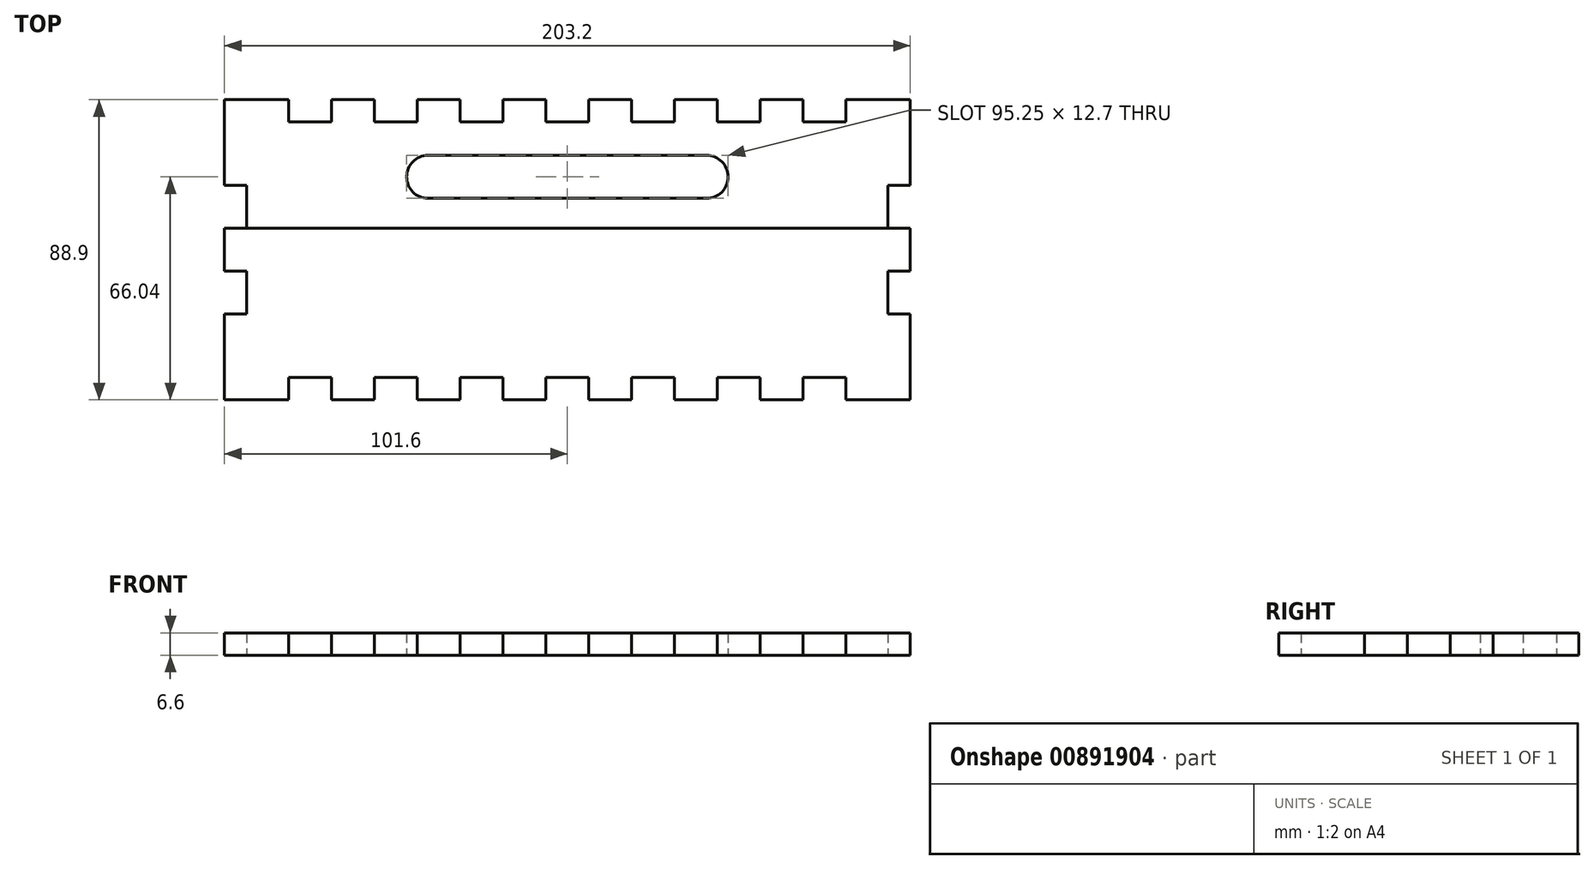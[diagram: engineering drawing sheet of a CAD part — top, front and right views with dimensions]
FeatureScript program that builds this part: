
annotation { "Feature Type Name" : "Feature", "Feature Type Description" : "" }
export const myFeature = defineFeature(function(context is Context, id is Id, definition is map)
    precondition{}
    {
        {
            var Q0;
            Q0=qCreatedBy(makeId("Top.planeOp"),FACE);
            var sketch = newSketch(context, id + "F0", { "sketchPlane" : qUnion([Q0])});
            skLineSegment(sketch, "E0.bottom", {"start": v(0, 0) * mm, "end": v(19.05, 0) * mm});
            skLineSegment(sketch, "E0.left", {"start": v(0, 0) * mm, "end": v(0, -25.4) * mm});
            skLineSegment(sketch, "E1", {"start": v(19.05, 0) * mm, "end": v(19.05, -6.6) * mm});
            skLineSegment(sketch, "E2", {"start": v(19.05, -6.6) * mm, "end": v(31.75, -6.6) * mm});
            skLineSegment(sketch, "E3", {"start": v(31.75, -6.6) * mm, "end": v(31.75, 0) * mm});
            skLineSegment(sketch, "E4", {"start": v(31.75, 0) * mm, "end": v(44.45, 0) * mm});
            skLineSegment(sketch, "E5", {"start": v(44.45, 0) * mm, "end": v(44.45, -6.6) * mm});
            skLineSegment(sketch, "E6", {"start": v(44.45, -6.6) * mm, "end": v(57.15, -6.6) * mm});
            skLineSegment(sketch, "E7", {"start": v(57.15, -6.6) * mm, "end": v(57.15, 0) * mm});
            skLineSegment(sketch, "E8", {"start": v(57.15, 0) * mm, "end": v(69.85, 0) * mm});
            skLineSegment(sketch, "E9", {"start": v(69.85, 0) * mm, "end": v(69.85, -6.6) * mm});
            skLineSegment(sketch, "E10", {"start": v(69.85, -6.6) * mm, "end": v(82.55, -6.6) * mm});
            skLineSegment(sketch, "E11", {"start": v(82.55, -6.6) * mm, "end": v(82.55, 0) * mm});
            skLineSegment(sketch, "E12.trimOffspring", {"start": v(82.55, 0) * mm, "end": v(95.25, 0) * mm});
            skLineSegment(sketch, "E13", {"start": v(95.25, 0) * mm, "end": v(95.25, -6.6) * mm});
            skLineSegment(sketch, "E14", {"start": v(95.25, -6.6) * mm, "end": v(107.95, -6.6) * mm});
            skLineSegment(sketch, "E15", {"start": v(107.95, -6.6) * mm, "end": v(107.95, 0) * mm});
            skLineSegment(sketch, "E16", {"start": v(107.95, 0) * mm, "end": v(120.65, 0) * mm});
            skLineSegment(sketch, "E17", {"start": v(120.65, 0) * mm, "end": v(120.65, -6.6) * mm});
            skLineSegment(sketch, "E18", {"start": v(120.65, -6.6) * mm, "end": v(133.35, -6.6) * mm});
            skLineSegment(sketch, "E19", {"start": v(133.35, -6.6) * mm, "end": v(133.35, 0) * mm});
            skLineSegment(sketch, "E20", {"start": v(133.35, 0) * mm, "end": v(146.05, 0) * mm});
            skLineSegment(sketch, "E21", {"start": v(146.05, 0) * mm, "end": v(146.05, -6.6) * mm});
            skLineSegment(sketch, "E22", {"start": v(146.05, -6.6) * mm, "end": v(158.75, -6.6) * mm});
            skLineSegment(sketch, "E23", {"start": v(158.75, -6.6) * mm, "end": v(158.75, 0) * mm});
            skLineSegment(sketch, "E24.trimOffspring", {"start": v(158.75, 0) * mm, "end": v(171.45, 0) * mm});
            skLineSegment(sketch, "E25", {"start": v(171.45, 0) * mm, "end": v(171.45, -6.6) * mm});
            skLineSegment(sketch, "E26", {"start": v(171.45, -6.6) * mm, "end": v(184.15, -6.6) * mm});
            skLineSegment(sketch, "E27", {"start": v(184.15, -6.6) * mm, "end": v(184.15, 0) * mm});
            skLineSegment(sketch, "E28.trimOffspring", {"start": v(184.15, 0) * mm, "end": v(203.2, 0) * mm});
            skLineSegment(sketch, "E29", {"start": v(0, -25.4) * mm, "end": v(6.6, -25.4) * mm});
            skLineSegment(sketch, "E30", {"start": v(6.6, -25.4) * mm, "end": v(6.6, -38.1) * mm});
            skLineSegment(sketch, "E31", {"start": v(6.6, -38.1) * mm, "end": v(0, -38.1) * mm});
            skLineSegment(sketch, "E32", {"start": v(0, -38.1) * mm, "end": v(0, -50.8) * mm});
            skLineSegment(sketch, "E33", {"start": v(0, -50.8) * mm, "end": v(6.6, -50.8) * mm});
            skLineSegment(sketch, "E34", {"start": v(6.6, -50.8) * mm, "end": v(6.6, -63.5) * mm});
            skLineSegment(sketch, "E35", {"start": v(6.6, -63.5) * mm, "end": v(0, -63.5) * mm});
            skLineSegment(sketch, "E36.trimOffspring", {"start": v(0, -63.5) * mm, "end": v(0, -88.9) * mm});
            skLineSegment(sketch, "E37", {"start": v(101.6, -6.6) * mm, "end": v(101.6, -6.6) * mm});
            skLineSegment(sketch, "E38", {"start": v(0, -44.45) * mm, "end": v(0, -44.45) * mm});
            skLineSegment(sketch, "E39.MirrorCS", {"start": v(203.2, 0) * mm, "end": v(203.2, -25.4) * mm});
            skLineSegment(sketch, "E40.MirrorCS", {"start": v(203.2, -25.4) * mm, "end": v(196.6, -25.4) * mm});
            skLineSegment(sketch, "E41.MirrorCS", {"start": v(196.6, -25.4) * mm, "end": v(196.6, -38.1) * mm});
            skLineSegment(sketch, "E42.MirrorCS", {"start": v(196.6, -38.1) * mm, "end": v(203.2, -38.1) * mm});
            skLineSegment(sketch, "E43.MirrorCS", {"start": v(203.2, -38.1) * mm, "end": v(203.2, -50.8) * mm});
            skLineSegment(sketch, "E44.MirrorCS", {"start": v(203.2, -50.8) * mm, "end": v(196.6, -50.8) * mm});
            skLineSegment(sketch, "E45.MirrorCS", {"start": v(196.6, -50.8) * mm, "end": v(196.6, -63.5) * mm});
            skLineSegment(sketch, "E46.MirrorCS", {"start": v(196.6, -63.5) * mm, "end": v(203.2, -63.5) * mm});
            skLineSegment(sketch, "E47.MirrorCS", {"start": v(203.2, -63.5) * mm, "end": v(203.2, -88.9) * mm});
            skLineSegment(sketch, "E48.MirrorCS", {"start": v(120.65, -88.9) * mm, "end": v(120.65, -82.3) * mm});
            skLineSegment(sketch, "E49.MirrorCS", {"start": v(19.05, -88.9) * mm, "end": v(19.05, -82.3) * mm});
            skLineSegment(sketch, "E50.MirrorCS", {"start": v(44.45, -88.9) * mm, "end": v(44.45, -82.3) * mm});
            skLineSegment(sketch, "E51.MirrorCS", {"start": v(69.85, -88.9) * mm, "end": v(69.85, -82.3) * mm});
            skLineSegment(sketch, "E52.MirrorCS", {"start": v(95.25, -88.9) * mm, "end": v(95.25, -82.3) * mm});
            skLineSegment(sketch, "E53.MirrorCS", {"start": v(107.95, -82.3) * mm, "end": v(107.95, -88.9) * mm});
            skLineSegment(sketch, "E54.MirrorCS", {"start": v(133.35, -82.3) * mm, "end": v(133.35, -88.9) * mm});
            skLineSegment(sketch, "E55.MirrorCS", {"start": v(31.75, -82.3) * mm, "end": v(31.75, -88.9) * mm});
            skLineSegment(sketch, "E56.MirrorCS", {"start": v(171.45, -88.9) * mm, "end": v(171.45, -82.3) * mm});
            skLineSegment(sketch, "E57.MirrorCS", {"start": v(146.05, -88.9) * mm, "end": v(146.05, -82.3) * mm});
            skLineSegment(sketch, "E58.MirrorCS", {"start": v(57.15, -82.3) * mm, "end": v(57.15, -88.9) * mm});
            skLineSegment(sketch, "E59.MirrorCS", {"start": v(82.55, -82.3) * mm, "end": v(82.55, -88.9) * mm});
            skLineSegment(sketch, "E60.MirrorCS", {"start": v(158.75, -82.3) * mm, "end": v(158.75, -88.9) * mm});
            skLineSegment(sketch, "E61.MirrorCS", {"start": v(184.15, -82.3) * mm, "end": v(184.15, -88.9) * mm});
            skLineSegment(sketch, "E62.MirrorCS", {"start": v(57.15, -88.9) * mm, "end": v(69.85, -88.9) * mm});
            skLineSegment(sketch, "E63.MirrorCS", {"start": v(82.55, -88.9) * mm, "end": v(95.25, -88.9) * mm});
            skLineSegment(sketch, "E64.MirrorCS", {"start": v(133.35, -88.9) * mm, "end": v(146.05, -88.9) * mm});
            skLineSegment(sketch, "E65.MirrorCS", {"start": v(95.25, -82.3) * mm, "end": v(107.95, -82.3) * mm});
            skLineSegment(sketch, "E66.MirrorCS", {"start": v(158.75, -88.9) * mm, "end": v(171.45, -88.9) * mm});
            skLineSegment(sketch, "E67.MirrorCS", {"start": v(107.95, -88.9) * mm, "end": v(120.65, -88.9) * mm});
            skLineSegment(sketch, "E68.MirrorCS", {"start": v(31.75, -88.9) * mm, "end": v(44.45, -88.9) * mm});
            skLineSegment(sketch, "E69.MirrorCS", {"start": v(69.85, -82.3) * mm, "end": v(82.55, -82.3) * mm});
            skLineSegment(sketch, "E70.MirrorCS", {"start": v(44.45, -82.3) * mm, "end": v(57.15, -82.3) * mm});
            skLineSegment(sketch, "E71.MirrorCS", {"start": v(19.05, -82.3) * mm, "end": v(31.75, -82.3) * mm});
            skLineSegment(sketch, "E72.MirrorCS", {"start": v(120.65, -82.3) * mm, "end": v(133.35, -82.3) * mm});
            skLineSegment(sketch, "E73.MirrorCS", {"start": v(171.45, -82.3) * mm, "end": v(184.15, -82.3) * mm});
            skLineSegment(sketch, "E74.MirrorCS", {"start": v(146.05, -82.3) * mm, "end": v(158.75, -82.3) * mm});
            skLineSegment(sketch, "E75.MirrorCS", {"start": v(0, -88.9) * mm, "end": v(19.05, -88.9) * mm});
            skLineSegment(sketch, "E76.MirrorCS", {"start": v(184.15, -88.9) * mm, "end": v(203.2, -88.9) * mm});
            skLineSegment(sketch, "E77", {"start": v(6.6, -38.1) * mm, "end": v(196.6, -38.1) * mm});
            skLineSegment(sketch, "E78.bottom", {"start": v(60.33, -16.5) * mm, "end": v(142.88, -16.5) * mm});
            skLineSegment(sketch, "E78.top", {"start": v(60.33, -29.2) * mm, "end": v(142.88, -29.2) * mm});
            skLineSegment(sketch, "E78.left", {"start": v(53.98, -22.86) * mm, "end": v(53.98, -22.86) * mm});
            skLineSegment(sketch, "E78.right", {"start": v(149.23, -22.86) * mm, "end": v(149.23, -22.86) * mm});
            skLineSegment(sketch, "E79", {"start": v(101.6, -16.5) * mm, "end": v(101.6, -6.6) * mm, "construction": true});
            skPoint(sketch, "E80.visualSharp", {"position": v(53.97, -16.5) * mm});
            skArc(sketch, "E80.filletArc", {"start": v(60.33, -16.5) * mm, "mid": v(55.83, -18.37) * mm, "end": v(53.98, -22.86) * mm});
            skPoint(sketch, "E81.visualSharp", {"position": v(53.98, -29.2) * mm});
            skArc(sketch, "E81.filletArc", {"start": v(53.98, -22.86) * mm, "mid": v(55.83, -27.35) * mm, "end": v(60.33, -29.2) * mm});
            skPoint(sketch, "E82.visualSharp", {"position": v(149.23, -16.5) * mm});
            skArc(sketch, "E82.filletArc", {"start": v(149.23, -22.86) * mm, "mid": v(147.37, -18.37) * mm, "end": v(142.88, -16.5) * mm});
            skPoint(sketch, "E83.visualSharp", {"position": v(149.23, -29.2) * mm});
            skArc(sketch, "E83.filletArc", {"start": v(142.88, -29.2) * mm, "mid": v(147.37, -27.35) * mm, "end": v(149.23, -22.86) * mm});
            skSolve(sketch);
        }
        {
            var Q0;
            Q0=makeQuery(id+"F0.imprint","IMPRINT",FACE,{"disambiguationData":[TD([[makeQuery(id+"F0.imprint","IMPRINT",EDGE,{"derivedFrom":sQuery(id+"F0.wireOp",EDGE,"E0.bottom")}),-1.0]])]});
            extrude(context, id + "F1", {"entities" : qUnion([Q0]), "depth" : 6.6 * mm, "offsetDistance" : 25.4 * mm});
        }
        {
            var Q0;
            Q0=makeQuery(id+"F0.imprint","IMPRINT",FACE,{"disambiguationData":[TD([[makeQuery(id+"F0.imprint","IMPRINT",EDGE,{"derivedFrom":sQuery(id+"F0.wireOp",EDGE,"E31")}),1.0]])]});
            extrude(context, id + "F2", {"entities" : qUnion([Q0]), "depth" : 6.6 * mm, "offsetDistance" : 25.4 * mm});
        }
    });
